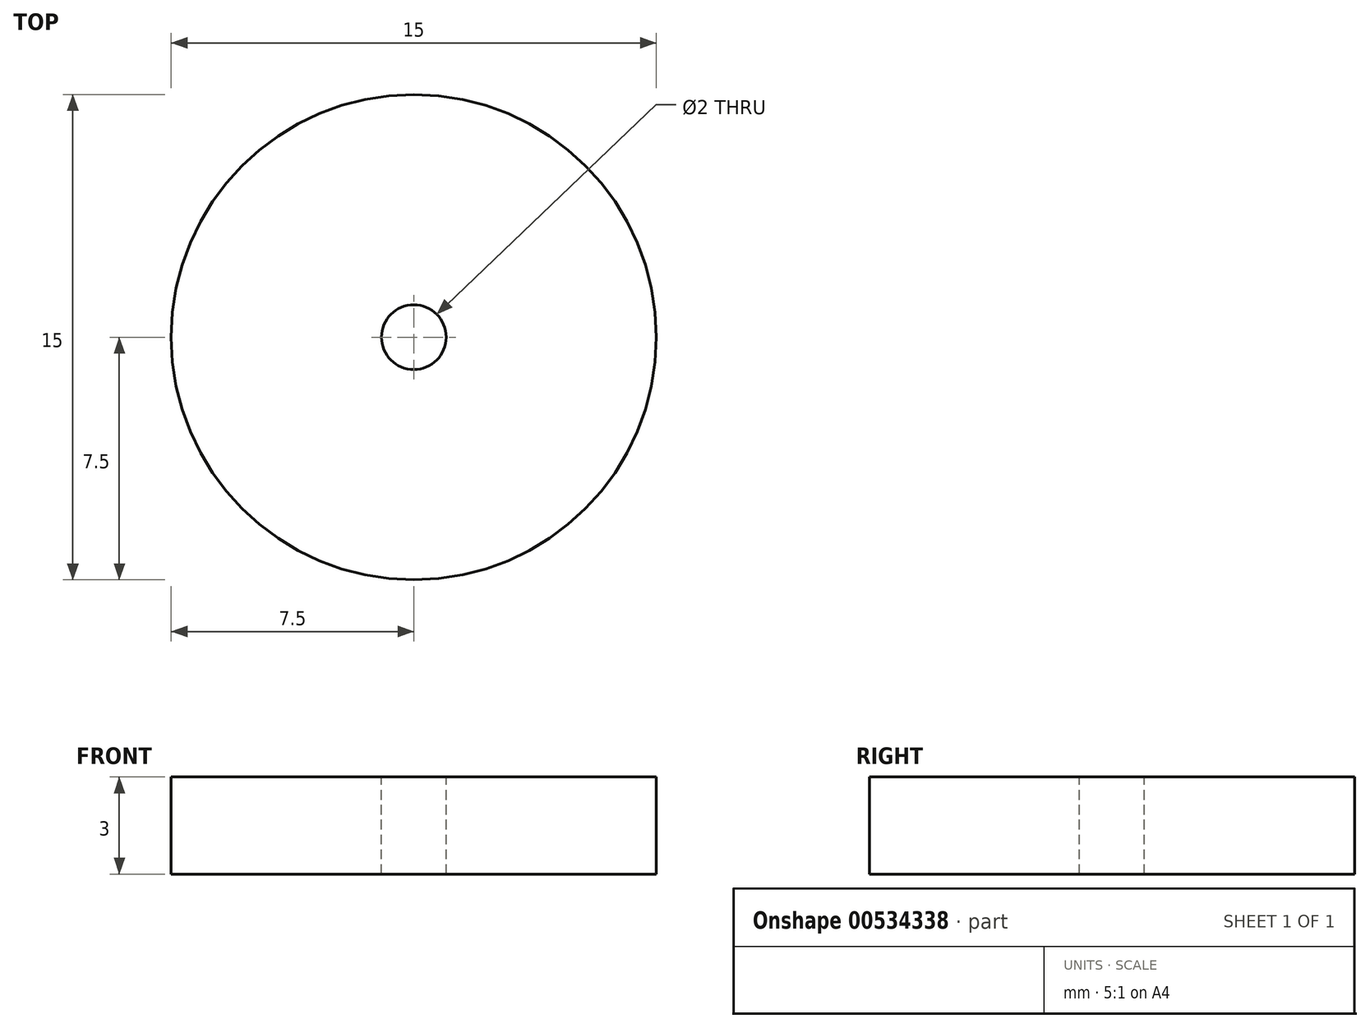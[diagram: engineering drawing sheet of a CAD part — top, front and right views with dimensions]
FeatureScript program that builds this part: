
annotation { "Feature Type Name" : "Feature", "Feature Type Description" : "" }
export const myFeature = defineFeature(function(context is Context, id is Id, definition is map)
    precondition{}
    {
        {
            var Q0;
            Q0=qCreatedBy(makeId("Top.planeOp"),FACE);
            var sketch = newSketch(context, id + "F0", { "sketchPlane" : qUnion([Q0])});
            skCircle(sketch, "E0", {"center": v(0, 0) * mm, "radius": 7.5 * mm});
            skSolve(sketch);
        }
        {
            var Q0;
            Q0 = qSketchRegion(id + "F0", true);
            extrude(context, id + "F1", {"entities" : qUnion([Q0]), "depth" : 3 * mm, "offsetDistance" : 25 * mm});
        }
        {
            var Q0;
            Q0=makeQuery(id+"F1.opExtrude","CAP_FACE",FACE,{"disambiguationData":[OSD([sQuery(id+"F0.wireOp",EDGE,"E0")])],"isStart":false});
            var sketch = newSketch(context, id + "F2", { "sketchPlane" : qUnion([Q0])});
            skCircle(sketch, "E1", {"center": v(0, 0) * mm, "radius": 1 * mm});
            skSolve(sketch);
        }
        {
            var Q0;
            Q0 = qSketchRegion(id + "F2", true);
            extrude(context, id + "F3", {"entities" : qUnion([Q0]), "operationType" : NewBodyOperationType.REMOVE, "endBound" : BoundingType.UP_TO_NEXT, "oppositeDirection" : true, "depth" : 25 * mm, "offsetDistance" : 25 * mm});
        }
    });
